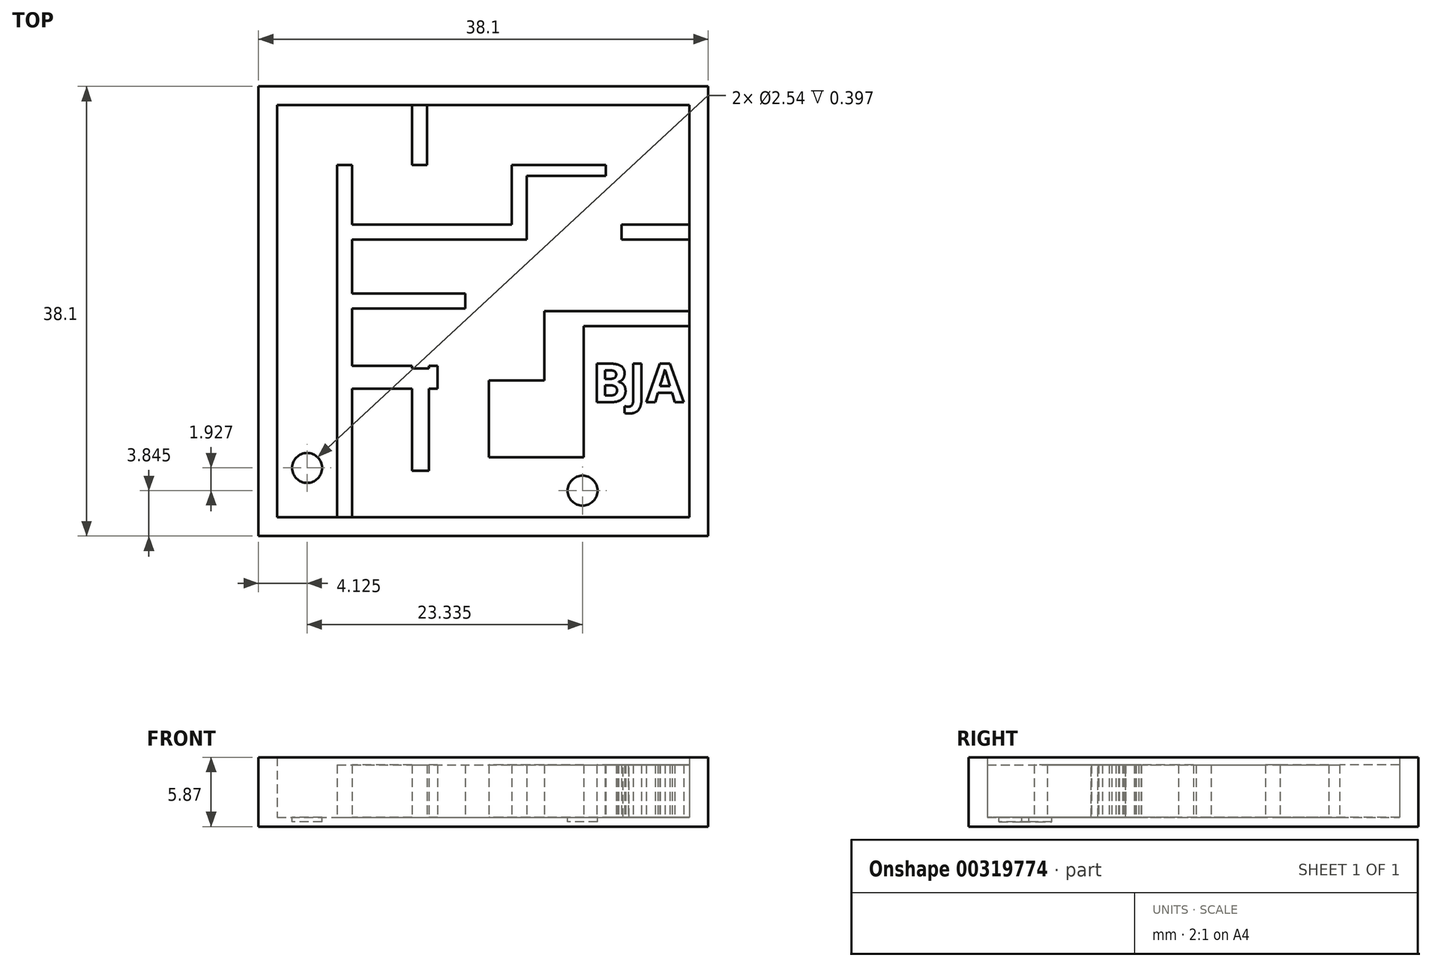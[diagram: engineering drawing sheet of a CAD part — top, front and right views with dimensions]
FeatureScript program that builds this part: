
annotation { "Feature Type Name" : "Feature", "Feature Type Description" : "" }
export const myFeature = defineFeature(function(context is Context, id is Id, definition is map)
    precondition{}
    {
        {
            var Q0;
            Q0=qCreatedBy(makeId("Top.planeOp"),FACE);
            var sketch = newSketch(context, id + "F0", { "sketchPlane" : qUnion([Q0])});
            skLineSegment(sketch, "E0.bottom", {"start": v(-19.57, 13.04) * mm, "end": v(18.53, 13.04) * mm});
            skLineSegment(sketch, "E0.top", {"start": v(-19.57, -25.06) * mm, "end": v(18.53, -25.06) * mm});
            skLineSegment(sketch, "E0.left", {"start": v(-19.57, 13.04) * mm, "end": v(-19.57, -25.06) * mm});
            skLineSegment(sketch, "E0.right", {"start": v(18.53, 13.04) * mm, "end": v(18.53, -25.06) * mm});
            skSolve(sketch);
        }
        {
            var Q0;
            Q0=makeQuery(id+"F0.imprint","IMPRINT",FACE,{"disambiguationData":[TD([[makeQuery(id+"F0.imprint","IMPRINT",EDGE,{"derivedFrom":sQuery(id+"F0.wireOp",EDGE,"E0.bottom")}),-1.0]])]});
            extrude(context, id + "F1", {"entities" : qUnion([Q0]), "depth" : 0.8 * mm});
        }
        {
            var Q0;
            Q0=makeQuery(id+"F1.opExtrude","CAP_FACE",FACE,{"disambiguationData":[OSD([sQuery(id+"F0.wireOp",EDGE,"E0.bottom"),sQuery(id+"F0.wireOp",EDGE,"E0.top"),sQuery(id+"F0.wireOp",EDGE,"E0.left"),sQuery(id+"F0.wireOp",EDGE,"E0.right")])],"isStart":false});
            var sketch = newSketch(context, id + "F2", { "sketchPlane" : qUnion([Q0])});
            skLineSegment(sketch, "E1.0", {"start": v(-17.98, 11.45) * mm, "end": v(16.94, 11.45) * mm});
            skLineSegment(sketch, "E1.1", {"start": v(-17.98, 11.45) * mm, "end": v(-17.98, -23.47) * mm});
            skLineSegment(sketch, "E1.2", {"start": v(-17.98, -23.47) * mm, "end": v(16.94, -23.47) * mm});
            skLineSegment(sketch, "E1.3", {"start": v(16.94, 11.45) * mm, "end": v(16.94, -23.47) * mm});
            skSolve(sketch);
        }
        {
            var Q0;
            Q0=makeQuery(id+"F2.imprint","IMPRINT",FACE,{"disambiguationData":[TD([[makeQuery(id+"F2.imprint","IMPRINT",EDGE,{"derivedFrom":sQuery(id+"F2.wireOp",EDGE,"E1.0")}),1.0]])]});
            extrude(context, id + "F3", {"entities" : qUnion([Q0]), "operationType" : NewBodyOperationType.ADD, "depth" : 5.08 * mm});
        }
        {
            var Q0;
            Q0=makeQuery(id+"F1.opExtrude","CAP_FACE",FACE,{"disambiguationData":[OSD([sQuery(id+"F0.wireOp",EDGE,"E0.bottom"),sQuery(id+"F0.wireOp",EDGE,"E0.top"),sQuery(id+"F0.wireOp",EDGE,"E0.left"),sQuery(id+"F0.wireOp",EDGE,"E0.right")])],"isStart":false});
            var sketch = newSketch(context, id + "F4", { "sketchPlane" : qUnion([Q0])});
            skLineSegment(sketch, "E2.bottom", {"start": v(-12.9, -23.47) * mm, "end": v(-11.63, -23.47) * mm});
            skLineSegment(sketch, "E2.top", {"start": v(-12.9, 6.37) * mm, "end": v(-11.63, 6.37) * mm});
            skLineSegment(sketch, "E2.left", {"start": v(-12.9, -23.47) * mm, "end": v(-12.9, 6.37) * mm});
            skLineSegment(sketch, "E2.right", {"start": v(-11.63, -23.47) * mm, "end": v(-11.63, 6.37) * mm});
            skLineSegment(sketch, "E3.top", {"start": v(4.64, -18.4) * mm, "end": v(8, -18.4) * mm});
            skLineSegment(sketch, "E3.left", {"start": v(4.64, -7.28) * mm, "end": v(4.64, -11.86) * mm});
            skLineSegment(sketch, "E3.right", {"start": v(8, -7.28) * mm, "end": v(8, -18.4) * mm});
            skLineSegment(sketch, "E4.top", {"start": v(4.64, -6.01) * mm, "end": v(16.94, -6.01) * mm});
            skLineSegment(sketch, "E4.left", {"start": v(4.64, -8.5) * mm, "end": v(4.64, -6.01) * mm});
            skLineSegment(sketch, "E4.right", {"start": v(16.94, -8.8) * mm, "end": v(16.94, -6.01) * mm});
            skLineSegment(sketch, "E5.bottom", {"start": v(-6.55, -10.86) * mm, "end": v(-5.13, -10.86) * mm});
            skLineSegment(sketch, "E5.top", {"start": v(-6.55, -19.52) * mm, "end": v(-5.13, -19.52) * mm});
            skLineSegment(sketch, "E5.left", {"start": v(-6.55, -10.64) * mm, "end": v(-6.55, -10.86) * mm});
            skLineSegment(sketch, "E5.right", {"start": v(-5.13, -10.64) * mm, "end": v(-5.13, -10.86) * mm});
            skLineSegment(sketch, "E6.bottom", {"start": v(-4.4, -10.64) * mm, "end": v(-5.13, -10.64) * mm});
            skLineSegment(sketch, "E6.top", {"start": v(-4.4, -12.56) * mm, "end": v(-5.13, -12.56) * mm});
            skLineSegment(sketch, "E6.left", {"start": v(-4.4, -10.64) * mm, "end": v(-4.4, -12.56) * mm});
            skLineSegment(sketch, "E6.right", {"start": v(-11.63, -10.64) * mm, "end": v(-11.63, -12.56) * mm});
            skLineSegment(sketch, "E7.bottom", {"start": v(4.64, -18.4) * mm, "end": v(-0.05, -18.4) * mm});
            skLineSegment(sketch, "E7.top", {"start": v(4.64, -11.86) * mm, "end": v(-0.05, -11.86) * mm});
            skLineSegment(sketch, "E7.right", {"start": v(-0.05, -18.4) * mm, "end": v(-0.05, -11.86) * mm});
            skLineSegment(sketch, "E8.bottom", {"start": v(-11.63, 1.34) * mm, "end": v(1.88, 1.34) * mm});
            skLineSegment(sketch, "E8.top", {"start": v(-11.63, 0.07) * mm, "end": v(3.15, 0.07) * mm});
            skLineSegment(sketch, "E8.left", {"start": v(-11.63, 1.34) * mm, "end": v(-11.63, 0.07) * mm});
            skLineSegment(sketch, "E8.right", {"start": v(3.15, 1.34) * mm, "end": v(3.15, 0.07) * mm});
            skLineSegment(sketch, "E9.bottom", {"start": v(-11.63, -5.78) * mm, "end": v(-2.05, -5.78) * mm});
            skLineSegment(sketch, "E9.top", {"start": v(-11.63, -4.5) * mm, "end": v(-2.05, -4.5) * mm});
            skLineSegment(sketch, "E9.left", {"start": v(-11.63, -5.78) * mm, "end": v(-11.63, -4.5) * mm});
            skLineSegment(sketch, "E9.right", {"start": v(-2.05, -5.78) * mm, "end": v(-2.05, -4.5) * mm});
            skLineSegment(sketch, "E10.bottom", {"start": v(16.94, 1.34) * mm, "end": v(11.18, 1.34) * mm});
            skLineSegment(sketch, "E10.top", {"start": v(16.94, 0.07) * mm, "end": v(11.18, 0.07) * mm});
            skLineSegment(sketch, "E10.left", {"start": v(16.94, 1.34) * mm, "end": v(16.94, 0.07) * mm});
            skLineSegment(sketch, "E10.right", {"start": v(11.18, 1.34) * mm, "end": v(11.18, 0.07) * mm});
            skLineSegment(sketch, "E11.bottom", {"start": v(-6.55, 11.45) * mm, "end": v(-5.28, 11.45) * mm});
            skLineSegment(sketch, "E11.left", {"start": v(-6.55, 11.45) * mm, "end": v(-6.55, 6.37) * mm});
            skLineSegment(sketch, "E11.right", {"start": v(-5.28, 1.34) * mm, "end": v(-5.28, 1.3) * mm});
            skPoint(sketch, "E12.oppositeSnap0", {"position": v(-6.55, 6.37) * mm});
            skLineSegment(sketch, "E12.top", {"start": v(1.88, 6.37) * mm, "end": v(3.15, 6.37) * mm});
            skLineSegment(sketch, "E12.left", {"start": v(1.88, 1.34) * mm, "end": v(1.88, 6.37) * mm});
            skLineSegment(sketch, "E12.right", {"start": v(3.15, 1.34) * mm, "end": v(3.15, 5.45) * mm});
            skLineSegment(sketch, "E13.bottom", {"start": v(3.15, 5.45) * mm, "end": v(9.86, 5.45) * mm});
            skLineSegment(sketch, "E13.top", {"start": v(3.15, 6.37) * mm, "end": v(9.86, 6.37) * mm});
            skLineSegment(sketch, "E13.right", {"start": v(9.86, 5.45) * mm, "end": v(9.86, 6.37) * mm});
            skLineSegment(sketch, "E14.trimOffspring", {"start": v(-5.13, -12.56) * mm, "end": v(-5.13, -19.52) * mm});
            skLineSegment(sketch, "E15.trimOffspring", {"start": v(-6.55, -12.56) * mm, "end": v(-6.55, -19.52) * mm});
            skLineSegment(sketch, "E16.trimOffspring", {"start": v(-6.55, -12.56) * mm, "end": v(-11.63, -12.56) * mm});
            skLineSegment(sketch, "E17.trimOffspring", {"start": v(-6.55, -10.64) * mm, "end": v(-11.63, -10.64) * mm});
            skLineSegment(sketch, "E18.trimOffspring", {"start": v(3.15, 6.37) * mm, "end": v(3.15, 6.37) * mm});
            skLineSegment(sketch, "E19.trimOffspring", {"start": v(-6.55, 1.34) * mm, "end": v(-6.55, 1.3) * mm});
            skLineSegment(sketch, "E20", {"start": v(-6.55, 6.37) * mm, "end": v(-5.28, 6.37) * mm});
            skLineSegment(sketch, "E21", {"start": v(-5.28, 6.37) * mm, "end": v(-5.28, 11.45) * mm});
            skLineSegment(sketch, "E22", {"start": v(-17.98, -23.47) * mm, "end": v(-12.9, -23.47) * mm});
            skCircle(sketch, "E23", {"center": v(-15.44, -19.29) * mm, "radius": 1.27 * mm});
            skPoint(sketch, "E23.centerSnap0", {"position": v(-15.44, -23.47) * mm});
            skCircle(sketch, "E24", {"center": v(7.9, -21.22) * mm, "radius": 1.27 * mm});
            skText(sketch, "E25", { "text": "BJA", "fontName": "OpenSans-Bold.ttf"});
            skLineSegment(sketch, "E26", {"start": v(8, -7.28) * mm, "end": v(16.94, -7.28) * mm});
            const initialGuessF4  = {"E25": [0.00869, -0.01372, 1, 0, 0.0033]};
            skSetInitialGuess(sketch, initialGuessF4);
            skSolve(sketch);
        }
        {
            var Q0;
            Q0=makeQuery(id+"F4.imprint","IMPRINT",FACE,{"disambiguationData":[TD([[makeQuery(id+"F4.imprint","IMPRINT",EDGE,{"derivedFrom":sQuery(id+"F4.wireOp",EDGE,"E23")}),1.0]])]});
            var Q1;
            Q1=makeQuery(id+"F4.imprint","IMPRINT",FACE,{"disambiguationData":[TD([[makeQuery(id+"F4.imprint","IMPRINT",EDGE,{"derivedFrom":sQuery(id+"F4.wireOp",EDGE,"E24")}),1.0]])]});
            extrude(context, id + "F5", {"entities" : qUnion([Q0, Q1]), "operationType" : NewBodyOperationType.REMOVE, "oppositeDirection" : true, "depth" : 0.4 * mm});
        }
        {
            var Q0;
            {var subQ4=sQuery(id+"F4.wireOp",EDGE,"E2.top");Q0=makeQuery(id+"F4.imprint","IMPRINT",FACE,{"disambiguationData":[TD([[makeQuery(id+"F4.imprint","IMPRINT",EDGE,{"derivedFrom":subQ4}),-1.0]])]});}
            var Q1;
            Q1=makeQuery(id+"F4.imprint","IMPRINT",FACE,{"disambiguationData":[TD([[makeQuery(id+"F4.imprint","IMPRINT",EDGE,{"derivedFrom":sQuery(id+"F4.wireOp",EDGE,"E11.left")}),1.0]])]});
            var Q2;
            Q2=makeQuery(id+"F4.imprint","IMPRINT",FACE,{"disambiguationData":[TD([[makeQuery(id+"F4.imprint","IMPRINT",EDGE,{"derivedFrom":sQuery(id+"F4.wireOp",EDGE,"E8.top")}),1.0]])]});
            var Q3;
            Q3=makeQuery(id+"F4.imprint","IMPRINT",FACE,{"disambiguationData":[TD([[makeQuery(id+"F4.imprint","IMPRINT",EDGE,{"derivedFrom":sQuery(id+"F4.wireOp",EDGE,"E9.bottom")}),1.0]])]});
            var Q4;
            Q4=makeQuery(id+"F4.imprint","IMPRINT",FACE,{"disambiguationData":[TD([[makeQuery(id+"F4.imprint","IMPRINT",EDGE,{"derivedFrom":sQuery(id+"F4.wireOp",EDGE,"E5.bottom")}),-1.0]])]});
            var Q5;
            Q5=makeQuery(id+"F4.imprint","IMPRINT",FACE,{"disambiguationData":[TD([[makeQuery(id+"F4.imprint","IMPRINT",EDGE,{"derivedFrom":sQuery(id+"F4.wireOp",EDGE,"E10.bottom")}),1.0]])]});
            var Q6;
            Q6=makeQuery(id+"F4.imprint","IMPRINT",FACE,{"disambiguationData":[TD([[makeQuery(id+"F4.imprint","IMPRINT",EDGE,{"derivedFrom":sQuery(id+"F4.wireOp",EDGE,"E3.top")}),1.0]])]});
            var Q7;
            Q7=makeQuery(id+"F4.imprint","IMPRINT",FACE,{"disambiguationData":[TD([[makeQuery(id+"F4.imprint","IMPRINT",EDGE,{"derivedFrom":sQuery(id+"F4.wireOp",EDGE,"E25.sketch_text.stroke-35")}),-1.0]])]});
            var Q8;
            Q8=makeQuery(id+"F4.imprint","IMPRINT",FACE,{"disambiguationData":[TD([[makeQuery(id+"F4.imprint","IMPRINT",EDGE,{"derivedFrom":sQuery(id+"F4.wireOp",EDGE,"E25.sketch_text.stroke-25")}),-1.0]])]});
            var Q9;
            Q9=makeQuery(id+"F4.imprint","IMPRINT",FACE,{"disambiguationData":[TD([[makeQuery(id+"F4.imprint","IMPRINT",EDGE,{"derivedFrom":sQuery(id+"F4.wireOp",EDGE,"E25.sketch_text.stroke-0")}),-1.0]])]});
            extrude(context, id + "F6", {"entities" : qUnion([Q0, Q1, Q2, Q3, Q4, Q5, Q6, Q7, Q8, Q9]), "operationType" : NewBodyOperationType.ADD, "depth" : 4.44 * mm});
        }
    });
